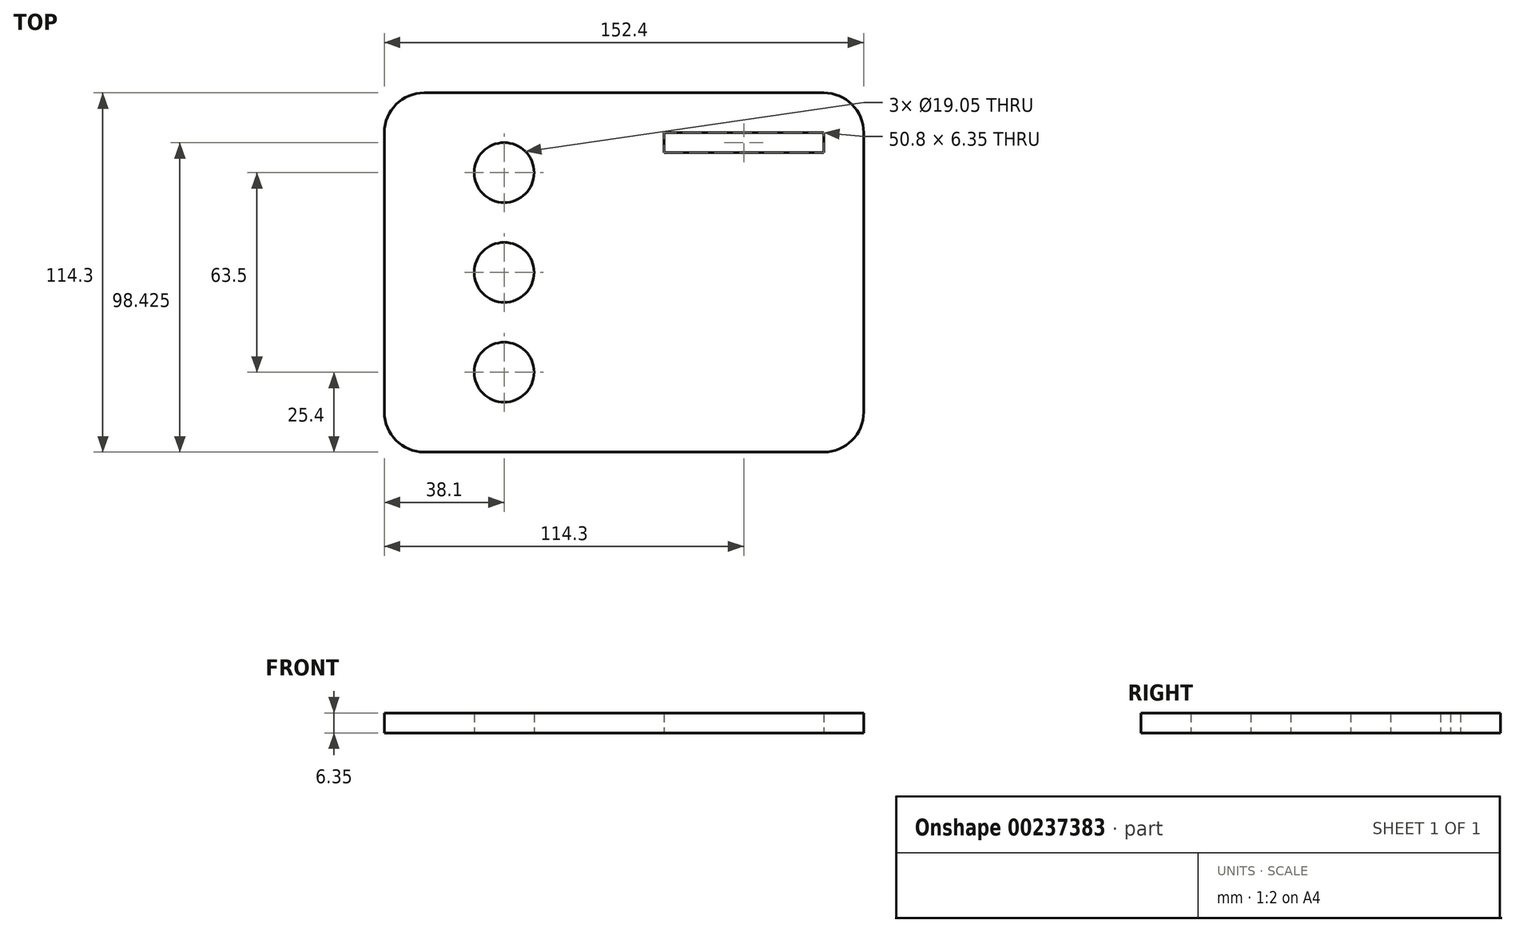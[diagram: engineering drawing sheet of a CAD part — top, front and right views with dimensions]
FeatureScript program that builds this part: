
annotation { "Feature Type Name" : "Feature", "Feature Type Description" : "" }
export const myFeature = defineFeature(function(context is Context, id is Id, definition is map)
    precondition{}
    {
        {
            var Q0;
            Q0=qCreatedBy(makeId("Top.planeOp"),FACE);
            var sketch = newSketch(context, id + "F0", { "sketchPlane" : qUnion([Q0])});
            skLineSegment(sketch, "E0.bottom", {"start": v(-76.2, 57.15) * mm, "end": v(76.2, 57.15) * mm});
            skLineSegment(sketch, "E0.top", {"start": v(-76.2, -57.15) * mm, "end": v(76.2, -57.15) * mm});
            skLineSegment(sketch, "E0.left", {"start": v(-76.2, 57.15) * mm, "end": v(-76.2, -57.15) * mm});
            skLineSegment(sketch, "E0.right", {"start": v(76.2, 57.15) * mm, "end": v(76.2, -57.15) * mm});
            skPoint(sketch, "E0.middle", {"position": v(0, 0) * mm});
            skSolve(sketch);
        }
        {
            var Q0;
            Q0 = qSketchRegion(id + "F0", true);
            extrude(context, id + "F1", {"entities" : qUnion([Q0]), "depth" : 6.35 * mm});
        }
        {
            var Q0;
            Q0=makeQuery(id+"F1.opExtrude","CAP_FACE",FACE,{"disambiguationData":[OSD([sQuery(id+"F0.wireOp",EDGE,"E0.bottom"),sQuery(id+"F0.wireOp",EDGE,"E0.top"),sQuery(id+"F0.wireOp",EDGE,"E0.left"),sQuery(id+"F0.wireOp",EDGE,"E0.right")])],"isStart":true});
            var sketch = newSketch(context, id + "F2", { "sketchPlane" : qUnion([Q0])});
            skCircle(sketch, "E1", {"center": v(-38.1, 0) * mm, "radius": 9.53 * mm});
            skCircle(sketch, "E2", {"center": v(-38.1, 31.75) * mm, "radius": 9.53 * mm});
            skCircle(sketch, "E3", {"center": v(-38.1, -31.75) * mm, "radius": 9.53 * mm});
            skSolve(sketch);
        }
        {
            var Q0;
            Q0 = qSketchRegion(id + "F2", true);
            extrude(context, id + "F3", {"entities" : qUnion([Q0]), "operationType" : NewBodyOperationType.REMOVE, "oppositeDirection" : true, "depth" : 25.4 * mm});
        }
        {
            var Q0;
            Q0=makeQuery(id+"F1.opExtrude","CAP_FACE",FACE,{"disambiguationData":[OSD([sQuery(id+"F0.wireOp",EDGE,"E0.bottom"),sQuery(id+"F0.wireOp",EDGE,"E0.top"),sQuery(id+"F0.wireOp",EDGE,"E0.left"),sQuery(id+"F0.wireOp",EDGE,"E0.right")])],"isStart":true});
            var sketch = newSketch(context, id + "F4", { "sketchPlane" : qUnion([Q0])});
            skSolve(sketch);
        }
        {
            var Q0;
            Q0=makeQuery(id+"F1.opExtrude","SWEPT_EDGE",EDGE,{"disambiguationData":[OSD([sQuery(id+"F0.wireOp",EDGE,"E0.top"),sQuery(id+"F0.wireOp",EDGE,"E0.left")])]});
            var Q1;
            Q1=makeQuery(id+"F1.opExtrude","SWEPT_EDGE",EDGE,{"disambiguationData":[OSD([sQuery(id+"F0.wireOp",EDGE,"E0.bottom"),sQuery(id+"F0.wireOp",EDGE,"E0.left")])]});
            var Q2;
            Q2=makeQuery(id+"F1.opExtrude","SWEPT_EDGE",EDGE,{"disambiguationData":[OSD([sQuery(id+"F0.wireOp",EDGE,"E0.bottom"),sQuery(id+"F0.wireOp",EDGE,"E0.right")])]});
            var Q3;
            Q3=makeQuery(id+"F1.opExtrude","SWEPT_EDGE",EDGE,{"disambiguationData":[OSD([sQuery(id+"F0.wireOp",EDGE,"E0.top"),sQuery(id+"F0.wireOp",EDGE,"E0.right")])]});
            fillet(context, id + "F5", {"entities" : qUnion([Q0, Q1, Q2, Q3]), "radius" : 12.7 * mm, "tangentPropagation" : true, "allowEdgeOverflow" : false});
        }
        {
            var Q0;
            Q0=makeQuery(id+"F4.imprint","IMPRINT",FACE,{"disambiguationData":[TD([[makeQuery(id+"F4.imprint","IMPRINT",EDGE,{"derivedFrom":makeQuery(id+"F1.opExtrude","CAP_EDGE",EDGE,{"disambiguationData":[OSD([sQuery(id+"F0.wireOp",EDGE,"E0.bottom")])],"isStart":true})}),1.0]])]});
            var sketch = newSketch(context, id + "F6", { "sketchPlane" : qUnion([Q0])});
            skLineSegment(sketch, "E4.bottom", {"start": v(63.5, -44.45) * mm, "end": v(12.7, -44.45) * mm});
            skLineSegment(sketch, "E4.top", {"start": v(63.5, -38.1) * mm, "end": v(12.7, -38.1) * mm});
            skLineSegment(sketch, "E4.left", {"start": v(63.5, -44.45) * mm, "end": v(63.5, -38.1) * mm});
            skLineSegment(sketch, "E4.right", {"start": v(12.7, -44.45) * mm, "end": v(12.7, -38.1) * mm});
            skSolve(sketch);
        }
        {
            var Q0;
            Q0 = qSketchRegion(id + "F6", true);
            extrude(context, id + "F7", {"entities" : qUnion([Q0]), "operationType" : NewBodyOperationType.REMOVE, "oppositeDirection" : true, "depth" : 25.4 * mm});
        }
    });
